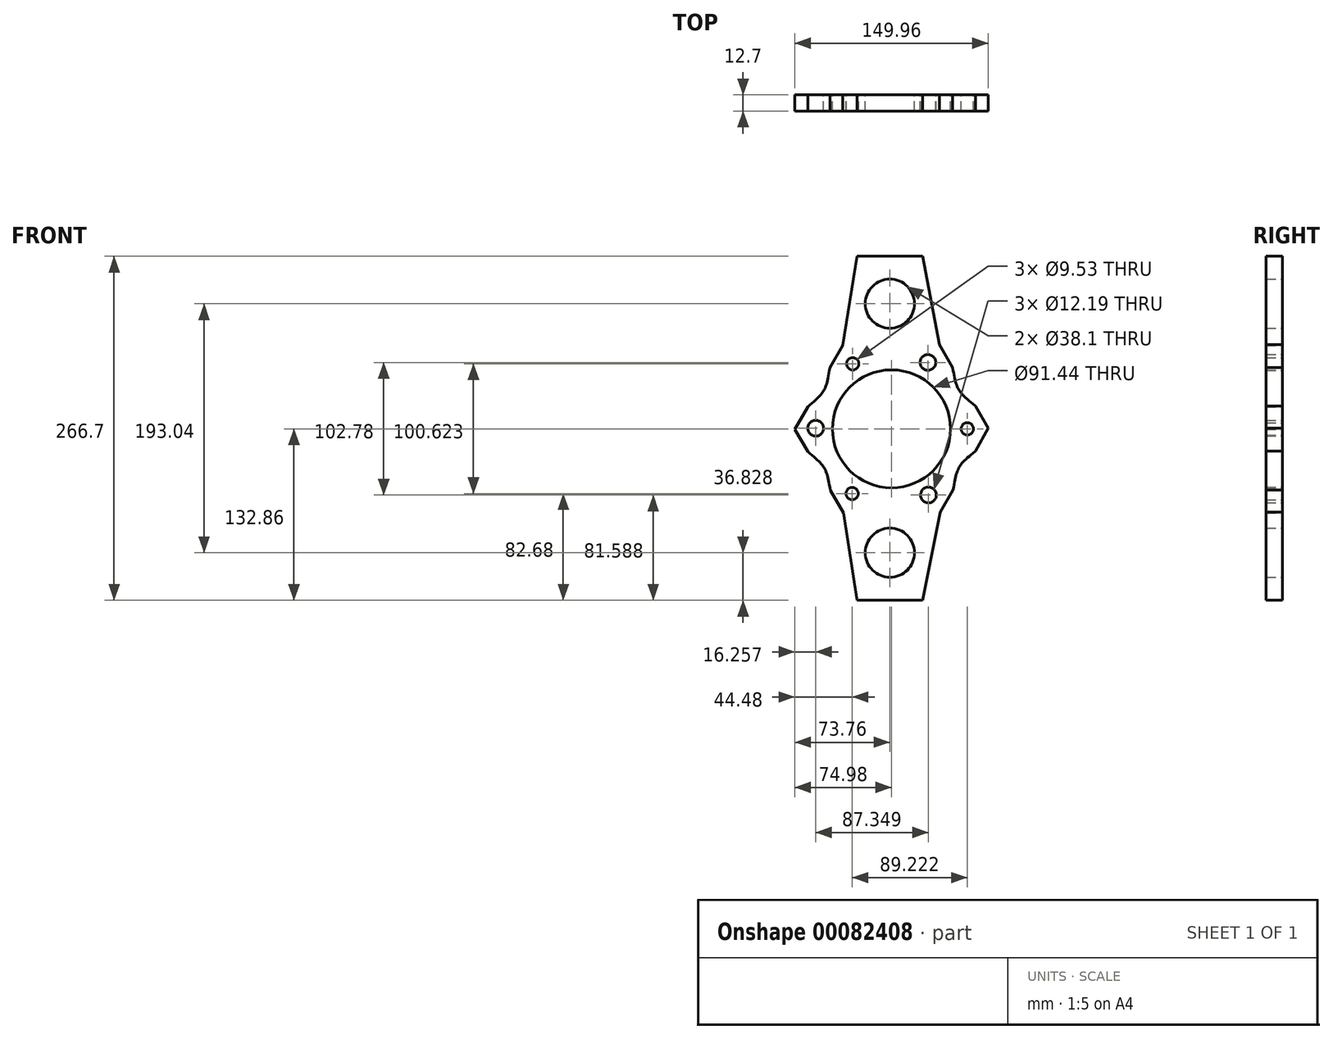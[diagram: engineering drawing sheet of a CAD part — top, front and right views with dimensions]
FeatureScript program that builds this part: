
annotation { "Feature Type Name" : "Feature", "Feature Type Description" : "" }
export const myFeature = defineFeature(function(context is Context, id is Id, definition is map)
    precondition{}
    {
        {
            var Q0;
            Q0=qCreatedBy(makeId("Front.planeOp"),FACE);
            var sketch = newSketch(context, id + "F0", { "sketchPlane" : qUnion([Q0])});
            skCircle(sketch, "E0", {"center": v(0, 0) * mm, "radius": 45.72 * mm});
            skCircle(sketch, "E1", {"center": v(28.2, 51.5) * mm, "radius": 6.1 * mm});
            skCircle(sketch, "E2", {"center": v(-58.72, 0.49) * mm, "radius": 6.1 * mm});
            skCircle(sketch, "E3", {"center": v(28.63, -51.27) * mm, "radius": 6.1 * mm});
            skCircle(sketch, "E4", {"center": v(-30.06, 50.44) * mm, "radius": 4.76 * mm});
            skCircle(sketch, "E5", {"center": v(58.72, 0) * mm, "radius": 4.76 * mm});
            skCircle(sketch, "E6", {"center": v(-30.5, -50.18) * mm, "radius": 4.76 * mm});
            skLineSegment(sketch, "E7.bottom", {"start": v(24.18, 133.84) * mm, "end": v(-26.62, 133.84) * mm});
            skLineSegment(sketch, "E7.top", {"start": v(24.18, -132.86) * mm, "end": v(-26.62, -132.86) * mm});
            skLineSegment(sketch, "E8", {"start": v(-26.62, 133.84) * mm, "end": v(-37.91, 64.7) * mm});
            skLineSegment(sketch, "E9", {"start": v(37.07, 65.18) * mm, "end": v(24.18, 133.84) * mm});
            skLineSegment(sketch, "E10", {"start": v(37.91, -64.7) * mm, "end": v(24.18, -132.86) * mm});
            skLineSegment(sketch, "E11", {"start": v(-26.62, -132.86) * mm, "end": v(-37.07, -65.18) * mm});
            skCircle(sketch, "E12", {"center": v(-1.22, 97) * mm, "radius": 19.05 * mm});
            skCircle(sketch, "E13", {"center": v(-1.22, -96.03) * mm, "radius": 19.05 * mm});
            skLineSegment(sketch, "E14.2", {"start": v(-37.07, -65.18) * mm, "end": v(-47.34, -47.65) * mm});
            skLineSegment(sketch, "E14.3", {"start": v(-74.98, -0.49) * mm, "end": v(-64.94, 17.17) * mm});
            skLineSegment(sketch, "E14.5", {"start": v(37.07, 65.18) * mm, "end": v(47.34, 47.65) * mm});
            skPoint(sketch, "E15.orphan", {"position": v(64.94, 37.5) * mm});
            skPoint(sketch, "E16.orphan", {"position": v(0, 74.98) * mm});
            skPoint(sketch, "E17.orphan", {"position": v(-64.94, 37.5) * mm});
            skPoint(sketch, "E18.orphan", {"position": v(-64.94, -37.5) * mm});
            skPoint(sketch, "E19.orphan", {"position": v(0, -74.98) * mm});
            skPoint(sketch, "E20.orphan", {"position": v(64.94, -37.5) * mm});
            skPoint(sketch, "E21.endDerivative.orphan", {"position": v(0, 58.72) * mm});
            skFitSpline(sketch, "E22", {"points": [v(47.34, 47.65) * mm, v(64.94, 17.63) * mm], "startDerivative": vector(9.97, -53.87) * mm, "endDerivative": vector(42.82, -36.2) * mm});
            skFitSpline(sketch, "E23", {"points": [v(64.94, -17.17) * mm, v(47.73, -47.42) * mm], "startDerivative": vector(-41.67, -35.57) * mm, "endDerivative": vector(-9.94, -55.18) * mm});
            skLineSegment(sketch, "E24", {"start": v(64.94, -17.17) * mm, "end": v(74.98, 0.49) * mm});
            skFitSpline(sketch, "E25", {"points": [v(-47.73, 47.42) * mm, v(-64.94, 17.17) * mm], "startDerivative": vector(-9.94, -55.18) * mm, "endDerivative": vector(-41.67, -35.57) * mm});
            skFitSpline(sketch, "E26", {"points": [v(-64.94, -17.63) * mm, v(-47.34, -47.65) * mm], "startDerivative": vector(42.82, -36.2) * mm, "endDerivative": vector(9.97, -53.87) * mm});
            skLineSegment(sketch, "E27.trimOffspring", {"start": v(-64.94, -17.63) * mm, "end": v(-74.98, -0.49) * mm});
            skPoint(sketch, "E28.orphan", {"position": v(-56.02, -32.83) * mm});
            skPoint(sketch, "E29.orphan", {"position": v(-56.45, 32.1) * mm});
            skLineSegment(sketch, "E30.trimOffspring", {"start": v(-47.73, 47.42) * mm, "end": v(-37.91, 64.7) * mm});
            skLineSegment(sketch, "E31.trimOffspring", {"start": v(64.94, 17.63) * mm, "end": v(74.98, 0.49) * mm});
            skPoint(sketch, "E32.orphan", {"position": v(56.02, 32.83) * mm});
            skLineSegment(sketch, "E33", {"start": v(37.91, -64.7) * mm, "end": v(47.73, -47.42) * mm});
            skCircle(sketch, "E34", {"center": v(0, 0) * mm, "radius": 58.72 * mm, "construction": true});
            skSolve(sketch);
        }
        {
            var Q0;
            Q0=makeQuery(id+"F0.imprint","IMPRINT",FACE,{"disambiguationData":[TD([[makeQuery(id+"F0.imprint","IMPRINT",EDGE,{"derivedFrom":sQuery(id+"F0.wireOp",EDGE,"E0")}),-1.0]])]});
            extrude(context, id + "F1", {"entities" : qUnion([Q0]), "depth" : 12.7 * mm});
        }
    });
